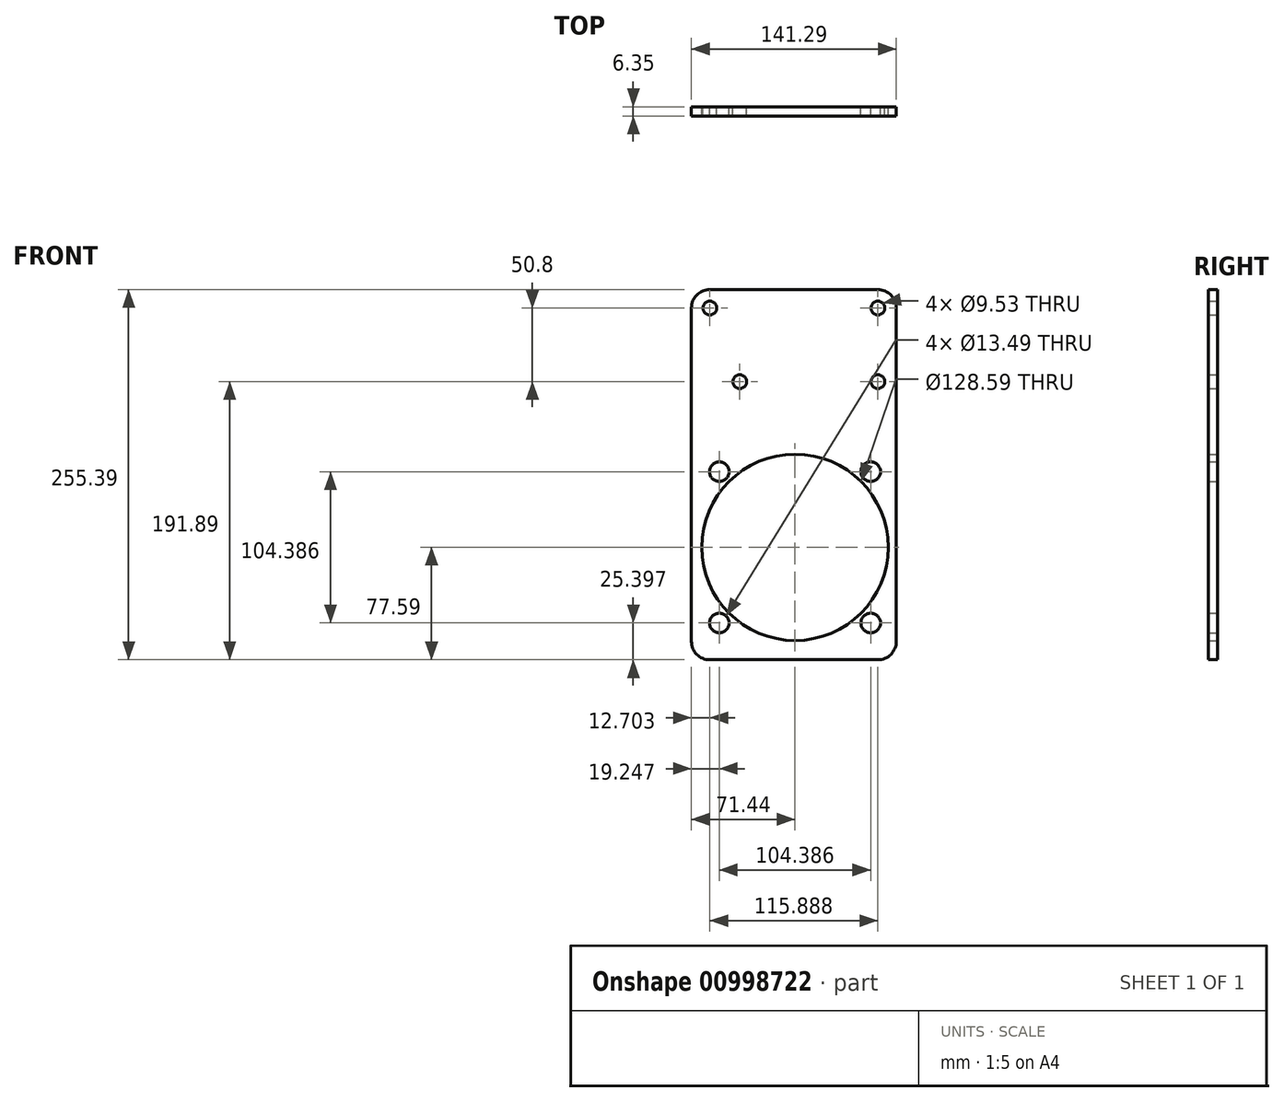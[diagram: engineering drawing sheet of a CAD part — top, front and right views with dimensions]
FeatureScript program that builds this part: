
annotation { "Feature Type Name" : "Feature", "Feature Type Description" : "" }
export const myFeature = defineFeature(function(context is Context, id is Id, definition is map)
    precondition{}
    {
        {
            var Q0;
            Q0=qCreatedBy(makeId("Front.planeOp"),FACE);
            var sketch = newSketch(context, id + "F0", { "sketchPlane" : qUnion([Q0])});
            skCircle(sketch, "E0", {"center": v(0, 0) * mm, "radius": 4.76 * mm});
            skCircle(sketch, "E1", {"center": v(-115.89, 0) * mm, "radius": 4.76 * mm});
            skCircle(sketch, "E2", {"center": v(0, -50.8) * mm, "radius": 4.76 * mm});
            skCircle(sketch, "E3", {"center": v(-95.25, -50.8) * mm, "radius": 4.76 * mm});
            skCircle(sketch, "E4", {"center": v(-57.15, -165.1) * mm, "radius": 64.3 * mm});
            skCircle(sketch, "E5", {"center": v(-57.15, -165.1) * mm, "radius": 73.81 * mm, "construction": true});
            skLineSegment(sketch, "E6.bottom", {"start": v(-109.34, -112.9) * mm, "end": v(-4.96, -112.9) * mm, "construction": true});
            skLineSegment(sketch, "E6.top", {"start": v(-109.34, -217.3) * mm, "end": v(-4.96, -217.3) * mm, "construction": true});
            skLineSegment(sketch, "E6.left", {"start": v(-109.34, -112.9) * mm, "end": v(-109.34, -217.3) * mm, "construction": true});
            skLineSegment(sketch, "E6.right", {"start": v(-4.96, -112.9) * mm, "end": v(-4.96, -217.3) * mm, "construction": true});
            skCircle(sketch, "E7", {"center": v(-4.96, -112.9) * mm, "radius": 6.75 * mm});
            skCircle(sketch, "E8", {"center": v(-109.34, -112.9) * mm, "radius": 6.75 * mm});
            skCircle(sketch, "E9", {"center": v(-109.34, -217.3) * mm, "radius": 6.75 * mm});
            skCircle(sketch, "E10", {"center": v(-4.96, -217.3) * mm, "radius": 6.75 * mm});
            skLineSegment(sketch, "E11.bottom", {"start": v(12.7, -242.7) * mm, "end": v(-128.59, -242.7) * mm});
            skLineSegment(sketch, "E11.top", {"start": v(12.7, 12.7) * mm, "end": v(-128.59, 12.7) * mm});
            skLineSegment(sketch, "E11.left", {"start": v(12.7, -242.7) * mm, "end": v(12.7, 12.7) * mm});
            skLineSegment(sketch, "E11.right", {"start": v(-128.59, -242.7) * mm, "end": v(-128.59, 12.7) * mm});
            skSolve(sketch);
        }
        {
            var Q0;
            Q0=makeQuery(id+"F0.imprint","IMPRINT",FACE,{"disambiguationData":[TD([[makeQuery(id+"F0.imprint","IMPRINT",EDGE,{"derivedFrom":sQuery(id+"F0.wireOp",EDGE,"E0")}),-1.0]])]});
            extrude(context, id + "F1", {"entities" : qUnion([Q0]), "depth" : 6.35 * mm, "offsetDistance" : 25.4 * mm});
        }
        {
            var Q0;
            Q0=makeQuery(id+"F1.opExtrude","SWEPT_EDGE",EDGE,{"disambiguationData":[OSD([sQuery(id+"F0.wireOp",EDGE,"E11.bottom"),sQuery(id+"F0.wireOp",EDGE,"E11.right")])]});
            var Q1;
            Q1=makeQuery(id+"F1.opExtrude","SWEPT_EDGE",EDGE,{"disambiguationData":[OSD([sQuery(id+"F0.wireOp",EDGE,"E11.bottom"),sQuery(id+"F0.wireOp",EDGE,"E11.left")])]});
            var Q2;
            Q2=makeQuery(id+"F1.opExtrude","SWEPT_EDGE",EDGE,{"disambiguationData":[OSD([sQuery(id+"F0.wireOp",EDGE,"E11.top"),sQuery(id+"F0.wireOp",EDGE,"E11.left")])]});
            var Q3;
            Q3=makeQuery(id+"F1.opExtrude","SWEPT_EDGE",EDGE,{"disambiguationData":[OSD([sQuery(id+"F0.wireOp",EDGE,"E11.top"),sQuery(id+"F0.wireOp",EDGE,"E11.right")])]});
            fillet(context, id + "F2", {"entities" : qUnion([Q0, Q1, Q2, Q3]), "radius" : 12.7 * mm, "tangentPropagation" : true, "allowEdgeOverflow" : false});
        }
    });
